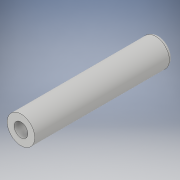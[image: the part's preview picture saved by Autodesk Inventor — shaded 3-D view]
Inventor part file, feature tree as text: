
AUTODESK INVENTOR PART (.ipt)
format: ipt  version: 2018 (Build 220112000, 112)  size: 104,960 bytes
history: native  units: in
note: dims shown in document units (in); Inventor stores cm internally (conversion verified against a paired STEP export)
features: extrude x1, thread x1, fillet x1, sketch x1
ambient origin geometry x8: Origin, YZ Plane, XZ Plane, XY Plane, X Axis, Y Axis, Z Axis, Center Point
bodies: Solid1 (feature_tree)
feature tree (4):
  extrude  "Extrusion1"  Depth=0.25in
  thread  "Thread1"  [1 undecoded]
  fillet  "Fillet1"  Radius=0.5in
  sketch  "Sketch1"  dims[d0=0.5in d1=0.25in d2=2.5in d3=0.0in d4=0.5in d5=0.0in d6=0.0625in]
note: 1 required parameter value undecoded (feature->parameter linkage not recoverable at this tier; creation-order binding heuristic only, values carry confidence <= 0.55)
